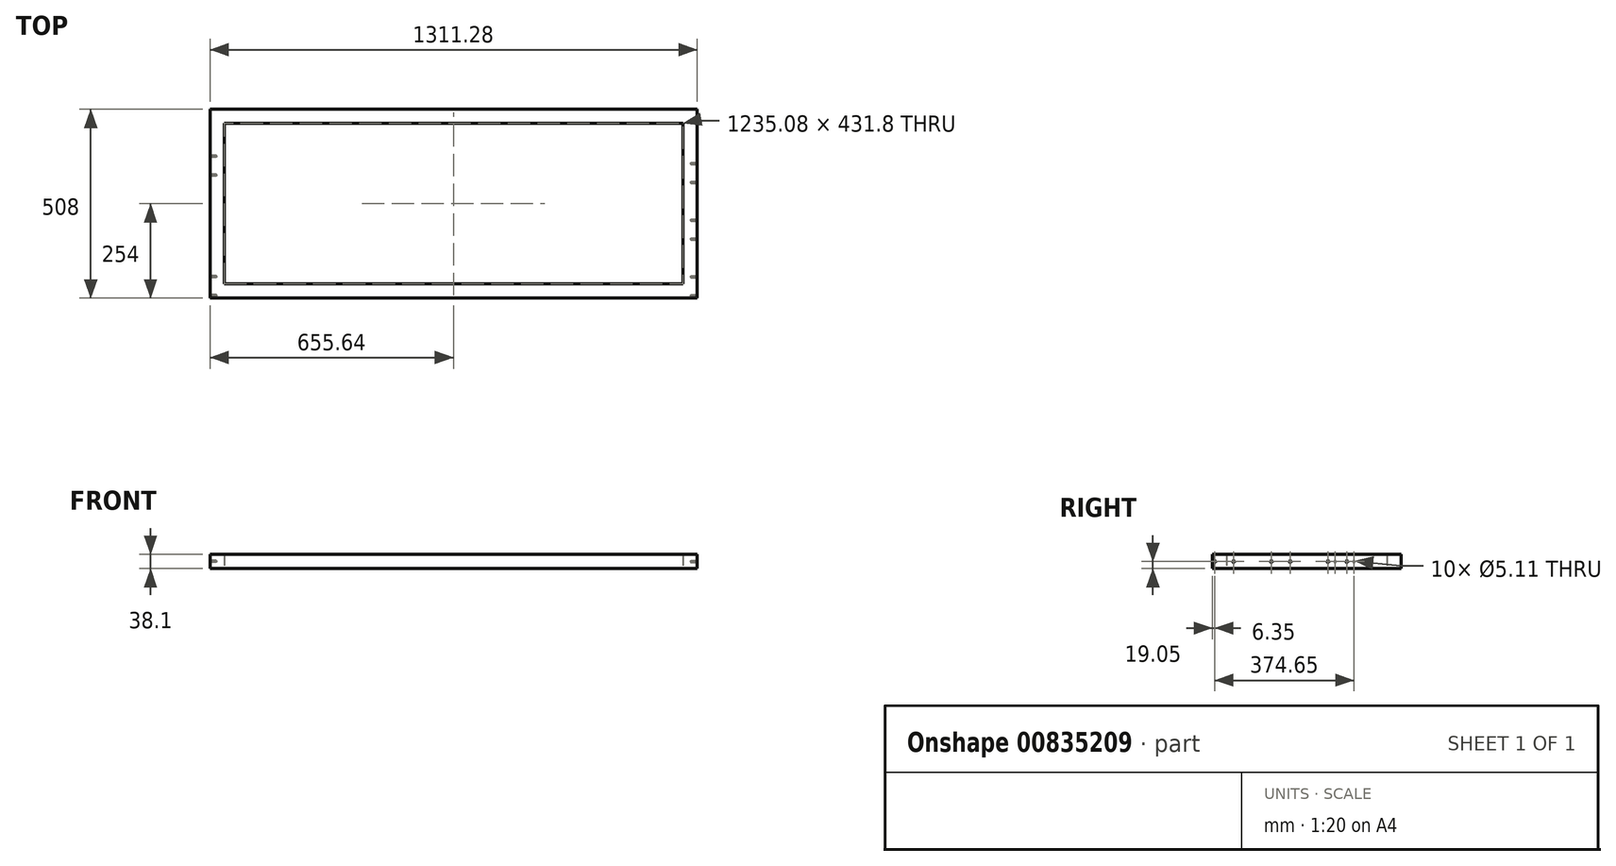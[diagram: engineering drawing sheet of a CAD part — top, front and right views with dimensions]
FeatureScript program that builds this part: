
annotation { "Feature Type Name" : "Feature", "Feature Type Description" : "" }
export const myFeature = defineFeature(function(context is Context, id is Id, definition is map)
    precondition{}
    {
        {
            var Q0;
            Q0=qCreatedBy(makeId("Top.planeOp"),FACE);
            var sketch = newSketch(context, id + "F0", { "sketchPlane" : qUnion([Q0])});
            skLineSegment(sketch, "E0.bottom", {"start": v(655.64, 254) * mm, "end": v(-655.64, 254) * mm});
            skLineSegment(sketch, "E0.top", {"start": v(655.64, -254) * mm, "end": v(-655.64, -254) * mm});
            skLineSegment(sketch, "E0.left", {"start": v(655.64, 254) * mm, "end": v(655.64, -254) * mm});
            skLineSegment(sketch, "E0.right", {"start": v(-655.64, 254) * mm, "end": v(-655.64, -254) * mm});
            skPoint(sketch, "E0.middle", {"position": v(0, 0) * mm});
            skLineSegment(sketch, "E1.bottom", {"start": v(617.54, 215.9) * mm, "end": v(-617.54, 215.9) * mm});
            skLineSegment(sketch, "E1.top", {"start": v(617.54, -215.9) * mm, "end": v(-617.54, -215.9) * mm});
            skLineSegment(sketch, "E1.left", {"start": v(617.54, 215.9) * mm, "end": v(617.54, -215.9) * mm});
            skLineSegment(sketch, "E1.right", {"start": v(-617.54, 215.9) * mm, "end": v(-617.54, -215.9) * mm});
            skSolve(sketch);
        }
        {
            var Q0;
            Q0 = qSketchRegion(id + "F0", true);
            extrude(context, id + "F1", {"entities" : qUnion([Q0]), "endBound" : BoundingType.SYMMETRIC, "depth" : 38.1 * mm, "offsetDistance" : 25.4 * mm});
        }
        {
            var Q0;
            Q0=makeQuery(id+"F1.opExtrude","SWEPT_FACE",FACE,{"disambiguationData":[OSD([sQuery(id+"F0.wireOp",EDGE,"E0.left")])]});
            var sketch = newSketch(context, id + "F2", { "sketchPlane" : qUnion([Q0])});
            skPoint(sketch, "E2", {"position": v(-247.65, 0) * mm});
            skPoint(sketch, "E3", {"position": v(-196.85, 0) * mm});
            skPoint(sketch, "E4", {"position": v(57.15, 0) * mm});
            skPoint(sketch, "E5", {"position": v(107.95, 0) * mm});
            skPoint(sketch, "E6", {"position": v(-95.25, 0) * mm});
            skPoint(sketch, "E7", {"position": v(-44.45, 0) * mm});
            skSolve(sketch);
        }
        {
            var Q0;
            Q0=makeQuery(id+"F1.opExtrude","SWEPT_FACE",FACE,{"disambiguationData":[OSD([sQuery(id+"F0.wireOp",EDGE,"E0.right")])]});
            var sketch = newSketch(context, id + "F3", { "sketchPlane" : qUnion([Q0])});
            skPoint(sketch, "E8", {"position": v(-76.2, 0) * mm});
            skPoint(sketch, "E9", {"position": v(-127, 0) * mm});
            skPoint(sketch, "E10", {"position": v(196.85, 0) * mm});
            skPoint(sketch, "E11", {"position": v(247.65, 0) * mm});
            skSolve(sketch);
        }
        {
            var Q0;
            Q0=sQuery(id+"F2.wireOp",VERTEX,"E4");
            var Q1;
            Q1=sQuery(id+"F2.wireOp",VERTEX,"E5");
            var Q2;
            Q2=sQuery(id+"F2.wireOp",VERTEX,"E3");
            var Q3;
            Q3=sQuery(id+"F2.wireOp",VERTEX,"E2");
            var Q4;
            Q4=sQuery(id+"F2.wireOp",VERTEX,"E7");
            var Q5;
            Q5=sQuery(id+"F2.wireOp",VERTEX,"E6");
            var Q6;
            Q6=sQuery(id+"F3.wireOp",VERTEX,"E11");
            var Q7;
            Q7=sQuery(id+"F3.wireOp",VERTEX,"E10");
            var Q8;
            Q8=sQuery(id+"F3.wireOp",VERTEX,"E8");
            var Q9;
            Q9=sQuery(id+"F3.wireOp",VERTEX,"E9");
            var Q10;
            Q10=makeQuery(id+"F1.opExtrude","SWEPT_BODY",BODY,{"disambiguationData":[OSD([sQuery(id+"F0.wireOp",EDGE,"E0.bottom"),sQuery(id+"F0.wireOp",EDGE,"E0.top"),sQuery(id+"F0.wireOp",EDGE,"E0.left"),sQuery(id+"F0.wireOp",EDGE,"E0.right"),sQuery(id+"F0.wireOp",EDGE,"E1.bottom"),sQuery(id+"F0.wireOp",EDGE,"E1.top"),sQuery(id+"F0.wireOp",EDGE,"E1.left"),sQuery(id+"F0.wireOp",EDGE,"E1.right")])]});
            hole(context, id + "F4", {"style" : HoleStyle.SIMPLE, "endStyle" : HoleEndStyle.BLIND, "standardTappedOrClearance" : lookupTablePath({ "standard" : "ANSI", "engagement" : "75%", "pitch" : "20 tpi", "size" : "1/4", "type" : "Tapped" }), "standardBlindInLast" : lookupTablePath({ "standard" : "ANSI", "engagement" : "75%", "pitch" : "20 tpi", "size" : "1/4", "type" : "Tapped" }), "holeDiameter" : 5.1 * mm, "majorDiameter" : 6.35 * mm, "showTappedDepth" : true, "holeDepth" : 16.51 * mm, "isTappedThrough" : true, "tappedDepth" : 12.7 * mm, "tapClearance" : 3, "startFromSketch" : true, "locations" : qUnion([Q0, Q1, Q2, Q3, Q4, Q5, Q6, Q7, Q8, Q9]), "scope" : qUnion([Q10])});
        }
    });
